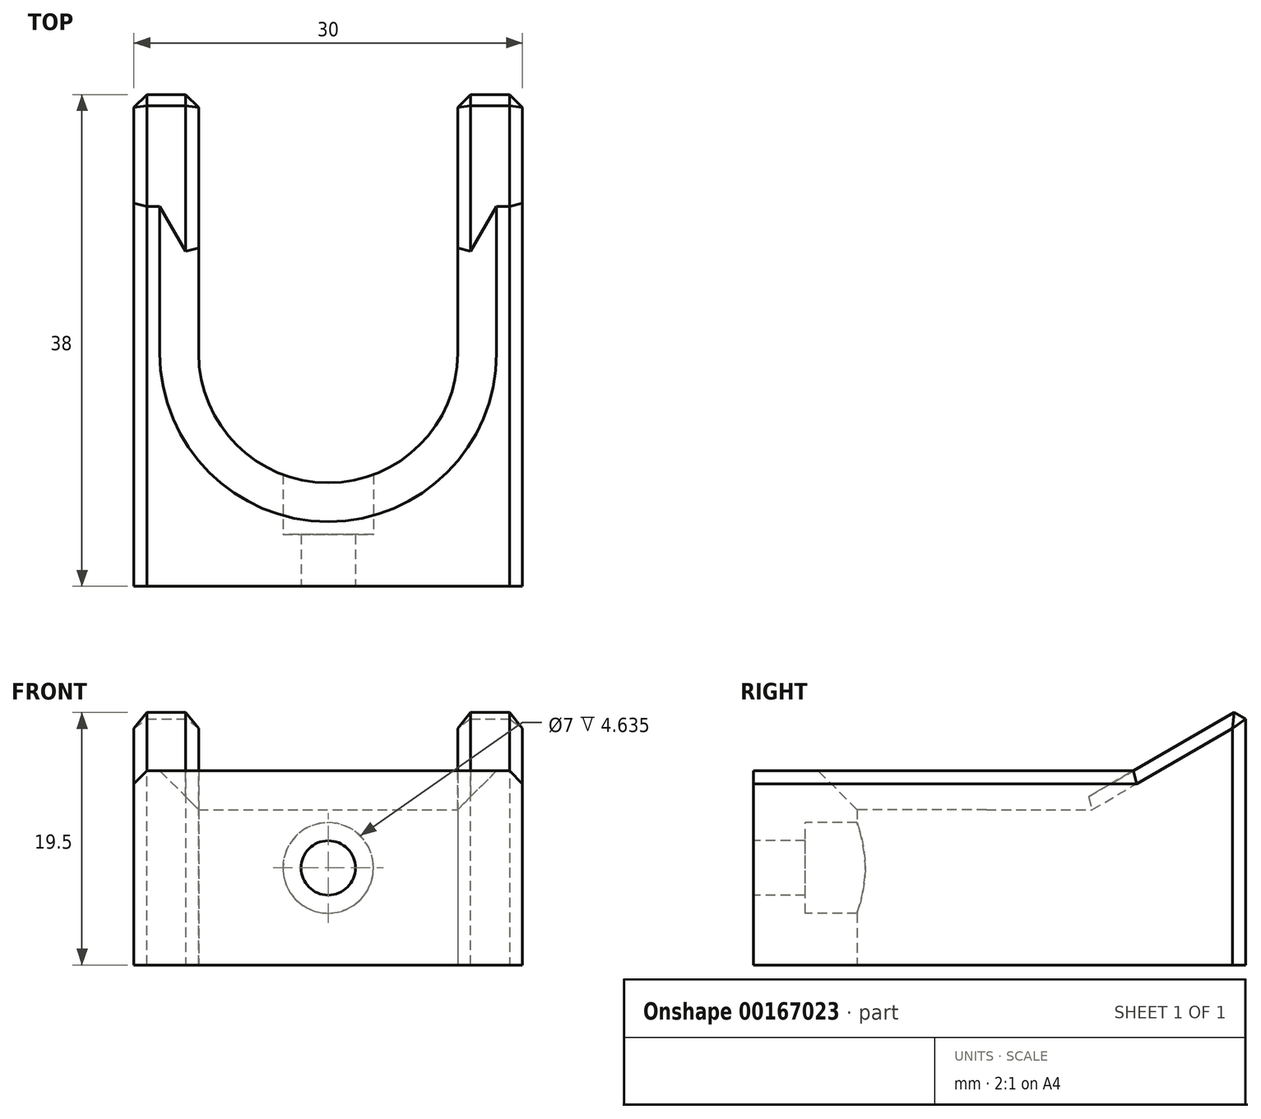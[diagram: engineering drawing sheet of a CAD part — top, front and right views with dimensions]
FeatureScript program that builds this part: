
annotation { "Feature Type Name" : "Feature", "Feature Type Description" : "" }
export const myFeature = defineFeature(function(context is Context, id is Id, definition is map)
    precondition{}
    {
        {
            var Q0;
            Q0=qCreatedBy(makeId("Top.planeOp"),FACE);
            var sketch = newSketch(context, id + "F0", { "sketchPlane" : qUnion([Q0])});
            skCircle(sketch, "E0", {"center": v(0, 0) * mm, "radius": 10 * mm});
            skCircle(sketch, "E1", {"center": v(0, 0) * mm, "radius": 15 * mm});
            skLineSegment(sketch, "E2", {"start": v(-10, 0) * mm, "end": v(-10, 20) * mm});
            skLineSegment(sketch, "E3", {"start": v(10, 0) * mm, "end": v(10, 20) * mm});
            skLineSegment(sketch, "E4", {"start": v(-15, 0) * mm, "end": v(-15, 20) * mm});
            skLineSegment(sketch, "E5", {"start": v(-15, 20) * mm, "end": v(-10, 20) * mm});
            skLineSegment(sketch, "E6", {"start": v(15, 0) * mm, "end": v(15, 20) * mm});
            skLineSegment(sketch, "E7", {"start": v(15, 20) * mm, "end": v(10, 20) * mm});
            skSolve(sketch);
        }
        {
            var Q0;
            {var subQ0=sQuery(id+"F0.wireOp",EDGE,"E4");Q0=makeQuery(id+"F0.imprint","IMPRINT",FACE,{"disambiguationData":[TD([[makeQuery(id+"F0.imprint","IMPRINT",EDGE,{"derivedFrom":subQ0}),-1.0]])]});}
            var Q1;
            {var subQ3=sQuery(id+"F0.wireOp",EDGE,"E2");var subQ7=sQuery(id+"F0.wireOp",EDGE,"E0");var subQ8=makeQuery(id+"F0.imprint","INTERSECT",VERTEX,{"derivedFrom":[subQ7,subQ3]});Q1=makeQuery(id+"F0.imprint","IMPRINT",FACE,{"disambiguationData":[TD([[makeQuery(id+"F0.imprint","IMPRINT",EDGE,{"disambiguationData":[TD([[subQ8,-1.0]])],"derivedFrom":subQ7}),-1.0]])]});}
            var Q2;
            {var subQ0=sQuery(id+"F0.wireOp",EDGE,"E6");Q2=makeQuery(id+"F0.imprint","IMPRINT",FACE,{"disambiguationData":[TD([[makeQuery(id+"F0.imprint","IMPRINT",EDGE,{"derivedFrom":subQ0}),1.0]])]});}
            extrude(context, id + "F1", {"entities" : qUnion([Q0, Q1, Q2]), "depth" : 15 * mm});
        }
        {
            var Q0;
            Q0=makeQuery(id+"F1.opExtrude","SWEPT_FACE",FACE,{"disambiguationData":[OSD([sQuery(id+"F0.wireOp",EDGE,"E4")])]});
            var sketch = newSketch(context, id + "F2", { "sketchPlane" : qUnion([Q0])});
            skLineSegment(sketch, "E8", {"start": v(-20, 15) * mm, "end": v(-20, 20) * mm});
            skLineSegment(sketch, "E9", {"start": v(-20, 20) * mm, "end": v(-11.34, 15) * mm});
            skSolve(sketch);
        }
        {
            var Q0;
            Q0=makeQuery(id+"F1.opExtrude","CAP_FACE",FACE,{"disambiguationData":[OSD([sQuery(id+"F0.wireOp",EDGE,"E0"),sQuery(id+"F0.wireOp",EDGE,"E1"),sQuery(id+"F0.wireOp",EDGE,"E2"),sQuery(id+"F0.wireOp",EDGE,"E3"),sQuery(id+"F0.wireOp",EDGE,"E4"),sQuery(id+"F0.wireOp",EDGE,"E5"),sQuery(id+"F0.wireOp",EDGE,"E6"),sQuery(id+"F0.wireOp",EDGE,"E7")])],"isStart":false});
            var sketch = newSketch(context, id + "F3", { "sketchPlane" : qUnion([Q0])});
            skPoint(sketch, "E10.endSnap0", {"position": v(0, -15) * mm});
            skLineSegment(sketch, "E11", {"start": v(15, 0) * mm, "end": v(15, -18) * mm});
            skLineSegment(sketch, "E12", {"start": v(15, -18) * mm, "end": v(-15, -18) * mm});
            skLineSegment(sketch, "E13", {"start": v(-15, -18) * mm, "end": v(-15, 0) * mm});
            skSolve(sketch);
        }
        {
            var Q0;
            Q0=makeQuery(id+"F3.imprint","IMPRINT",FACE,{"disambiguationData":[TD([[makeQuery(id+"F3.imprint","IMPRINT",EDGE,{"derivedFrom":sQuery(id+"F3.wireOp",EDGE,"E11")}),-1.0]])]});
            extrude(context, id + "F4", {"entities" : qUnion([Q0]), "operationType" : NewBodyOperationType.ADD, "oppositeDirection" : true, "depth" : 15 * mm});
        }
        {
            var Q0;
            {var subQ0=sQuery(id+"F2.wireOp",EDGE,"E8");Q0=makeQuery(id+"F2.imprint","IMPRINT",FACE,{"disambiguationData":[TD([[makeQuery(id+"F2.imprint","IMPRINT",EDGE,{"derivedFrom":subQ0}),-1.0]])]});}
            extrude(context, id + "F5", {"entities" : qUnion([Q0]), "operationType" : NewBodyOperationType.ADD, "oppositeDirection" : true, "depth" : 5 * mm});
        }
        {
            var Q0;
            Q0=makeQuery(id+"F4.boolean.opBoolean","MERGE",FACE,{"derivedFrom":[makeQuery(id+"F1.opExtrude","SWEPT_FACE",FACE,{"disambiguationData":[OSD([sQuery(id+"F0.wireOp",EDGE,"E6")])]}),makeQuery(id+"F4.opExtrude","SWEPT_FACE",FACE,{"disambiguationData":[OSD([sQuery(id+"F3.wireOp",EDGE,"E11")])]})]});
            var sketch = newSketch(context, id + "F6", { "sketchPlane" : qUnion([Q0])});
            skLineSegment(sketch, "E14", {"start": v(20, 15) * mm, "end": v(20, 20) * mm});
            skLineSegment(sketch, "E15", {"start": v(20, 20) * mm, "end": v(11.34, 15) * mm});
            skSolve(sketch);
        }
        {
            var Q0;
            {var subQ0=sQuery(id+"F6.wireOp",EDGE,"E14");Q0=makeQuery(id+"F6.imprint","IMPRINT",FACE,{"disambiguationData":[TD([[makeQuery(id+"F6.imprint","IMPRINT",EDGE,{"derivedFrom":subQ0}),1.0]])]});}
            extrude(context, id + "F7", {"entities" : qUnion([Q0]), "oppositeDirection" : true, "depth" : 5 * mm});
        }
        {
            var Q0;
            Q0=makeQuery(id+"F7.opExtrude","SWEPT_BODY",BODY,{"disambiguationData":[OSD([sQuery(id+"F0.wireOp",EDGE,"E6"),sQuery(id+"F3.wireOp",EDGE,"E11"),sQuery(id+"F6.wireOp",EDGE,"E14"),sQuery(id+"F6.wireOp",EDGE,"E15")])]});
            var Q1;
            Q1=makeQuery(id+"F1.opExtrude","SWEPT_BODY",BODY,{"disambiguationData":[OSD([sQuery(id+"F0.wireOp",EDGE,"E0"),sQuery(id+"F0.wireOp",EDGE,"E1"),sQuery(id+"F0.wireOp",EDGE,"E2"),sQuery(id+"F0.wireOp",EDGE,"E3"),sQuery(id+"F0.wireOp",EDGE,"E4"),sQuery(id+"F0.wireOp",EDGE,"E5"),sQuery(id+"F0.wireOp",EDGE,"E6"),sQuery(id+"F0.wireOp",EDGE,"E7")])]});
            booleanBodies(context, id + "F8", {"operationType" : BooleanOperationType.UNION, "tools" : qUnion([Q0, Q1])});
        }
        {
            var Q0;
            Q0=makeQuery(id+"F1.opExtrude","CAP_EDGE",EDGE,{"disambiguationData":[OSD([sQuery(id+"F0.wireOp",EDGE,"E2")])],"isStart":false});
            var Q1;
            Q1=makeQuery(id+"F1.opExtrude","CAP_EDGE",EDGE,{"disambiguationData":[OSD([sQuery(id+"F0.wireOp",EDGE,"E0")])],"isStart":false});
            chamfer(context, id + "F9", {"entities" : qUnion([Q0, Q1]), "width" : 3 * mm, "tangentPropagation" : true});
        }
        {
            var Q0;
            Q0=makeQuery(id+"F5.boolean.opBoolean","MERGE",EDGE,{"derivedFrom":[makeQuery(id+"F1.opExtrude","SWEPT_EDGE",EDGE,{"disambiguationData":[OSD([sQuery(id+"F0.wireOp",EDGE,"E2"),sQuery(id+"F0.wireOp",EDGE,"E5")])]}),makeQuery(id+"F5.opExtrude","CAP_EDGE",EDGE,{"disambiguationData":[OSD([sQuery(id+"F2.wireOp",EDGE,"E8")])],"isStart":false})]});
            var Q1;
            Q1=makeQuery(id+"F5.opExtrude","SWEPT_EDGE",EDGE,{"disambiguationData":[OSD([sQuery(id+"F2.wireOp",EDGE,"E8"),sQuery(id+"F2.wireOp",EDGE,"E9")])]});
            var Q2;
            Q2=makeQuery(id+"F5.boolean.opBoolean","MERGE",EDGE,{"derivedFrom":[makeQuery(id+"F1.opExtrude","SWEPT_EDGE",EDGE,{"disambiguationData":[OSD([sQuery(id+"F0.wireOp",EDGE,"E4"),sQuery(id+"F0.wireOp",EDGE,"E5")])]}),makeQuery(id+"F5.opExtrude","CAP_EDGE",EDGE,{"disambiguationData":[OSD([sQuery(id+"F2.wireOp",EDGE,"E8")])],"isStart":true})]});
            var Q3;
            Q3=makeQuery(id+"F8.opBoolean","MERGE",EDGE,{"derivedFrom":[makeQuery(id+"F1.opExtrude","SWEPT_EDGE",EDGE,{"disambiguationData":[OSD([sQuery(id+"F0.wireOp",EDGE,"E3"),sQuery(id+"F0.wireOp",EDGE,"E7")])]}),makeQuery(id+"F7.opExtrude","CAP_EDGE",EDGE,{"disambiguationData":[OSD([sQuery(id+"F6.wireOp",EDGE,"E14")])],"isStart":false})]});
            var Q4;
            Q4=makeQuery(id+"F7.opExtrude","SWEPT_EDGE",EDGE,{"disambiguationData":[OSD([sQuery(id+"F6.wireOp",EDGE,"E14"),sQuery(id+"F6.wireOp",EDGE,"E15")])]});
            var Q5;
            Q5=makeQuery(id+"F8.opBoolean","MERGE",EDGE,{"derivedFrom":[makeQuery(id+"F1.opExtrude","SWEPT_EDGE",EDGE,{"disambiguationData":[OSD([sQuery(id+"F0.wireOp",EDGE,"E6"),sQuery(id+"F0.wireOp",EDGE,"E7")])]}),makeQuery(id+"F7.opExtrude","CAP_EDGE",EDGE,{"disambiguationData":[OSD([sQuery(id+"F6.wireOp",EDGE,"E14")])],"isStart":true})]});
            var Q6;
            Q6=makeQuery(id+"F4.boolean.opBoolean","MERGE",EDGE,{"derivedFrom":[makeQuery(id+"F1.opExtrude","CAP_EDGE",EDGE,{"disambiguationData":[OSD([sQuery(id+"F0.wireOp",EDGE,"E6")])],"isStart":false}),makeQuery(id+"F4.opExtrude","CAP_EDGE",EDGE,{"disambiguationData":[OSD([sQuery(id+"F3.wireOp",EDGE,"E11")])],"isStart":true})]});
            var Q7;
            Q7=makeQuery(id+"F7.opExtrude","CAP_EDGE",EDGE,{"disambiguationData":[OSD([sQuery(id+"F6.wireOp",EDGE,"E15")])],"isStart":true});
            var Q8;
            Q8=makeQuery(id+"F5.opExtrude","CAP_EDGE",EDGE,{"disambiguationData":[OSD([sQuery(id+"F2.wireOp",EDGE,"E9")])],"isStart":true});
            var Q9;
            Q9=makeQuery(id+"F4.boolean.opBoolean","MERGE",EDGE,{"derivedFrom":[makeQuery(id+"F1.opExtrude","CAP_EDGE",EDGE,{"disambiguationData":[OSD([sQuery(id+"F0.wireOp",EDGE,"E4")])],"isStart":false}),makeQuery(id+"F4.opExtrude","CAP_EDGE",EDGE,{"disambiguationData":[OSD([sQuery(id+"F3.wireOp",EDGE,"E13")])],"isStart":true})]});
            var Q10;
            Q10=makeQuery(id+"F7.opExtrude","CAP_EDGE",EDGE,{"disambiguationData":[OSD([sQuery(id+"F6.wireOp",EDGE,"E15")])],"isStart":false});
            var Q11;
            Q11=makeQuery(id+"F5.opExtrude","CAP_EDGE",EDGE,{"disambiguationData":[OSD([sQuery(id+"F2.wireOp",EDGE,"E9")])],"isStart":false});
            chamfer(context, id + "F10", {"entities" : qUnion([Q0, Q1, Q2, Q3, Q4, Q5, Q6, Q7, Q8, Q9, Q10, Q11]), "width" : 1 * mm, "tangentPropagation" : true});
        }
        {
            var Q0;
            Q0=makeQuery(id+"F4.opExtrude","SWEPT_FACE",FACE,{"disambiguationData":[OSD([sQuery(id+"F3.wireOp",EDGE,"E12")])]});
            cPlane(context, id + "F11", {"entities" : qUnion([Q0]), "cplaneType" : CPlaneType.OFFSET, "offset" : 9 * mm, "oppositeDirection" : true, "width" : 150 * mm, "height" : 150 * mm});
        }
        {
            var Q0;
            Q0=qCreatedBy(id+"F11.planeOp",FACE);
            var sketch = newSketch(context, id + "F12", { "sketchPlane" : qUnion([Q0])});
            skLineSegment(sketch, "E16", {"start": v(0, 0) * mm, "end": v(0, 7.5) * mm});
            skSolve(sketch);
        }
        {
            var Q0;
            Q0=sQuery(id+"F12.wireOp",VERTEX,"E16.end");
            var Q1;
            Q1=makeQuery(id+"F7.opExtrude","SWEPT_BODY",BODY,{"disambiguationData":[OSD([sQuery(id+"F0.wireOp",EDGE,"E6"),sQuery(id+"F3.wireOp",EDGE,"E11"),sQuery(id+"F6.wireOp",EDGE,"E14"),sQuery(id+"F6.wireOp",EDGE,"E15")])]});
            hole(context, id + "F13", {"style" : HoleStyle.C_BORE, "endStyle" : HoleEndStyle.THROUGH, "oppositeDirection" : true, "holeDiameter" : 4.2 * mm, "cBoreDiameter" : 7 * mm, "cBoreDepth" : 4 * mm, "locations" : qUnion([Q0]), "scope" : qUnion([Q1]), "isTappedThrough" : true, "startStyle" : HoleStartStyle.PART});
        }
    });
